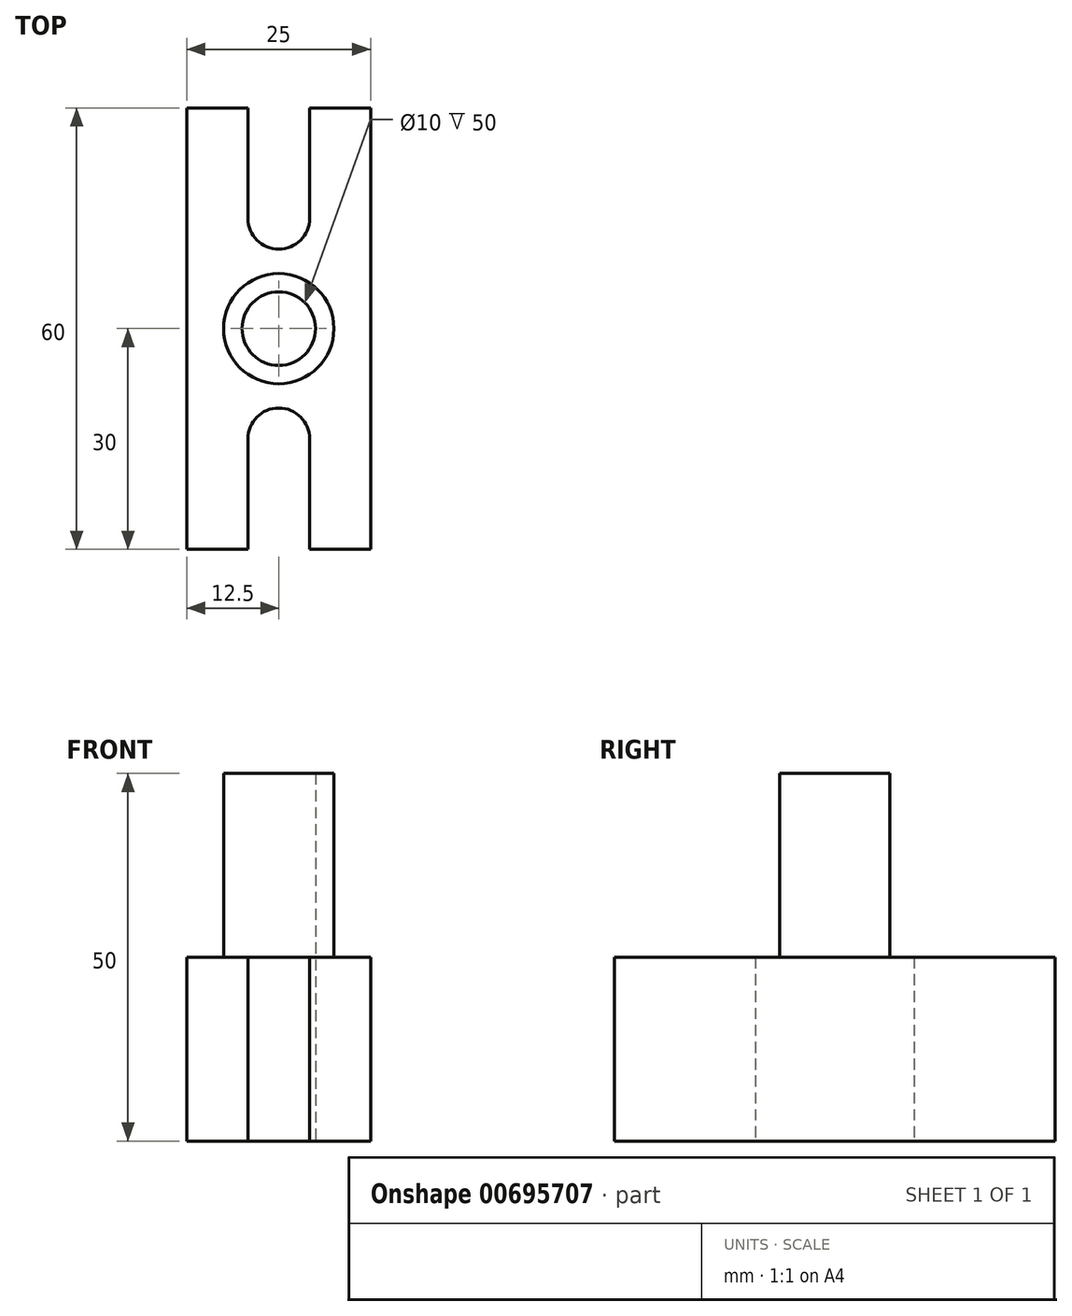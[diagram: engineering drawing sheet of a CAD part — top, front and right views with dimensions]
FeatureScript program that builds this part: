
annotation { "Feature Type Name" : "Feature", "Feature Type Description" : "" }
export const myFeature = defineFeature(function(context is Context, id is Id, definition is map)
    precondition{}
    {
        {
            var Q0;
            Q0=qCreatedBy(makeId("Top.planeOp"),FACE);
            var sketch = newSketch(context, id + "F0", { "sketchPlane" : qUnion([Q0])});
            skLineSegment(sketch, "E0.bottom", {"start": v(12.5, -30) * mm, "end": v(4.2, -30) * mm});
            skLineSegment(sketch, "E0.top", {"start": v(12.5, 30) * mm, "end": v(4.2, 30) * mm});
            skLineSegment(sketch, "E0.left", {"start": v(12.5, -30) * mm, "end": v(12.5, 30) * mm});
            skLineSegment(sketch, "E0.right", {"start": v(-12.5, -30) * mm, "end": v(-12.5, 30) * mm});
            skPoint(sketch, "E0.middle", {"position": v(0, 0) * mm});
            skLineSegment(sketch, "E1", {"start": v(-4.2, 30) * mm, "end": v(-4.2, 15) * mm});
            skLineSegment(sketch, "E2", {"start": v(4.2, 15) * mm, "end": v(4.2, 30) * mm});
            skLineSegment(sketch, "E3", {"start": v(-4.2, -30) * mm, "end": v(-4.2, -15) * mm});
            skLineSegment(sketch, "E4", {"start": v(4.2, -15) * mm, "end": v(4.2, -30) * mm});
            skArc(sketch, "E5", {"start": v(4.2, -15) * mm, "mid": v(0, -10.8) * mm, "end": v(-4.2, -15) * mm});
            skArc(sketch, "E6", {"start": v(-4.2, 15) * mm, "mid": v(0, 10.8) * mm, "end": v(4.2, 15) * mm});
            skLineSegment(sketch, "E7.trimOffspring", {"start": v(-4.2, 30) * mm, "end": v(-12.5, 30) * mm});
            skLineSegment(sketch, "E8.trimOffspring", {"start": v(-4.2, -30) * mm, "end": v(-12.5, -30) * mm});
            skCircle(sketch, "E9", {"center": v(0, 0) * mm, "radius": 5 * mm});
            skSolve(sketch);
        }
        {
            var Q0;
            Q0 = qSketchRegion(id + "F0", true);
            extrude(context, id + "F1", {"entities" : qUnion([Q0]), "depth" : 25 * mm, "offsetDistance" : 25 * mm});
        }
        {
            var Q0;
            Q0=makeQuery(id+"F1.opExtrude","CAP_FACE",FACE,{"disambiguationData":[OSD([sQuery(id+"F0.wireOp",EDGE,"E0.bottom"),sQuery(id+"F0.wireOp",EDGE,"E0.top"),sQuery(id+"F0.wireOp",EDGE,"E0.left"),sQuery(id+"F0.wireOp",EDGE,"E0.right"),sQuery(id+"F0.wireOp",EDGE,"E1"),sQuery(id+"F0.wireOp",EDGE,"E2"),sQuery(id+"F0.wireOp",EDGE,"E3"),sQuery(id+"F0.wireOp",EDGE,"E4"),sQuery(id+"F0.wireOp",EDGE,"E5"),sQuery(id+"F0.wireOp",EDGE,"E6"),sQuery(id+"F0.wireOp",EDGE,"E7.trimOffspring"),sQuery(id+"F0.wireOp",EDGE,"E8.trimOffspring")])],"isStart":false});
            var sketch = newSketch(context, id + "F2", { "sketchPlane" : qUnion([Q0])});
            skCircle(sketch, "E10", {"center": v(0, 0) * mm, "radius": 5 * mm});
            skCircle(sketch, "E11", {"center": v(0, 0) * mm, "radius": 7.5 * mm});
            skSolve(sketch);
        }
        {
            var Q0;
            Q0 = qSketchRegion(id + "F2", true);
            extrude(context, id + "F3", {"entities" : qUnion([Q0]), "operationType" : NewBodyOperationType.ADD, "depth" : 25 * mm, "offsetDistance" : 25 * mm});
        }
    });
